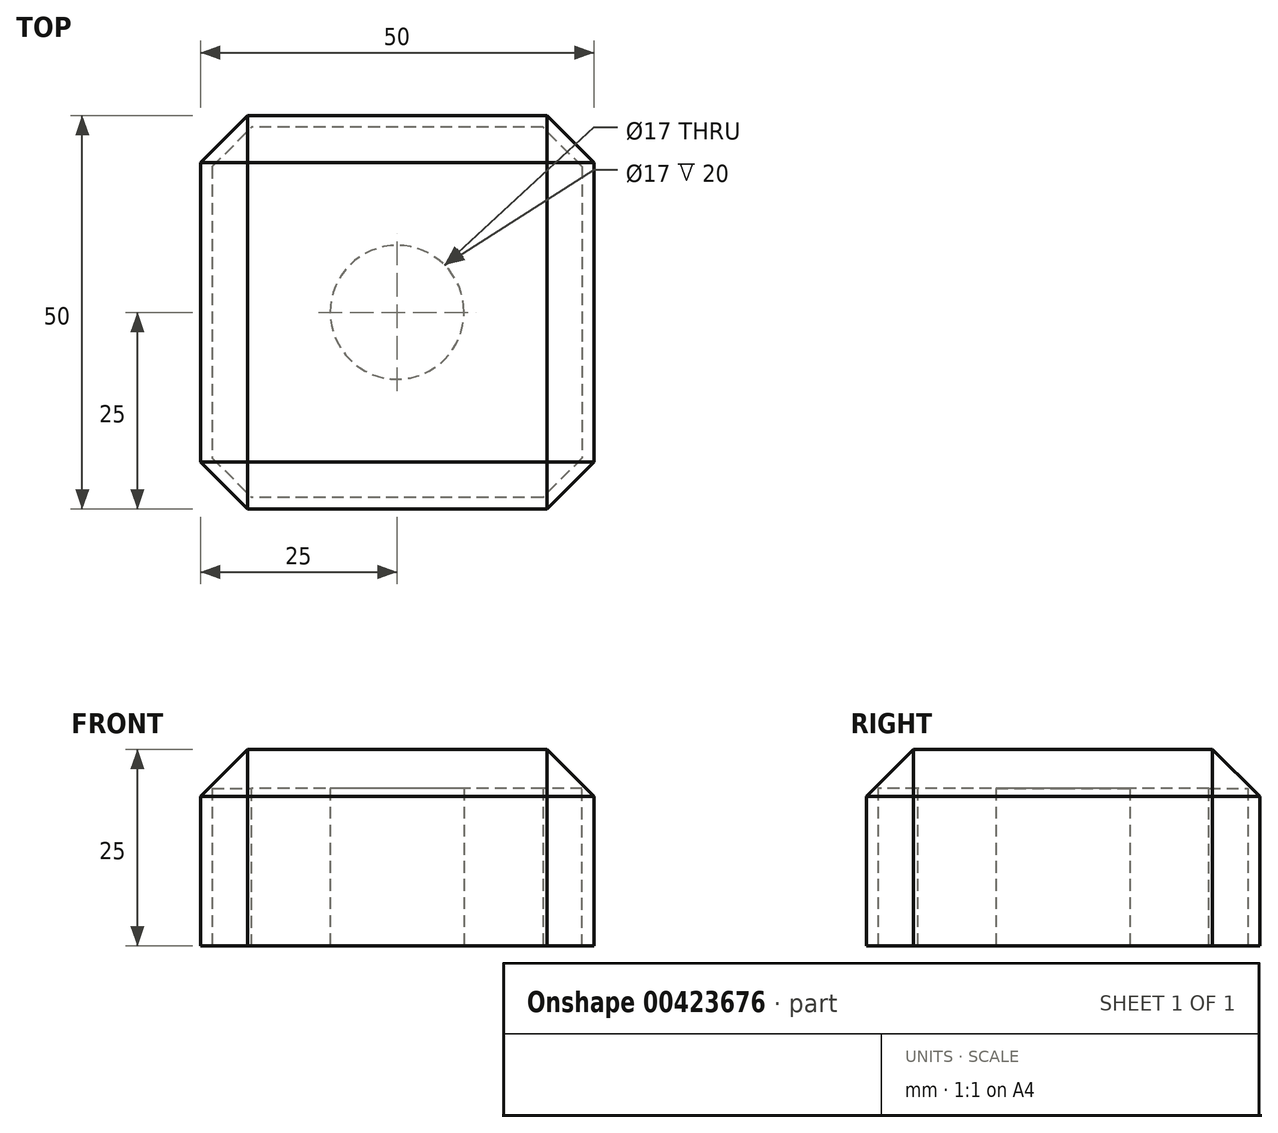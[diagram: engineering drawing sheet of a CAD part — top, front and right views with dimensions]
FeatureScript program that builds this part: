
annotation { "Feature Type Name" : "Feature", "Feature Type Description" : "" }
export const myFeature = defineFeature(function(context is Context, id is Id, definition is map)
    precondition{}
    {
        {
            var Q0;
            Q0=qCreatedBy(makeId("Top.planeOp"),FACE);
            var sketch = newSketch(context, id + "F0", { "sketchPlane" : qUnion([Q0])});
            skCircle(sketch, "E0", {"center": v(0, 0) * mm, "radius": 8.5 * mm});
            skLineSegment(sketch, "E1.bottom", {"start": v(23.5, 23.5) * mm, "end": v(-23.5, 23.5) * mm});
            skLineSegment(sketch, "E1.top", {"start": v(23.5, -23.5) * mm, "end": v(-23.5, -23.5) * mm});
            skLineSegment(sketch, "E1.left", {"start": v(23.5, 23.5) * mm, "end": v(23.5, -23.5) * mm});
            skLineSegment(sketch, "E1.right", {"start": v(-23.5, 23.5) * mm, "end": v(-23.5, -23.5) * mm});
            skSolve(sketch);
        }
        {
            var Q0;
            Q0=qCreatedBy(makeId("Top.planeOp"),FACE);
            var sketch = newSketch(context, id + "F1", { "sketchPlane" : qUnion([Q0])});
            skLineSegment(sketch, "E2.bottom", {"start": v(25, 25) * mm, "end": v(-25, 25) * mm});
            skLineSegment(sketch, "E2.top", {"start": v(25, -25) * mm, "end": v(-25, -25) * mm});
            skLineSegment(sketch, "E2.left", {"start": v(25, 25) * mm, "end": v(25, -25) * mm});
            skLineSegment(sketch, "E2.right", {"start": v(-25, 25) * mm, "end": v(-25, -25) * mm});
            skPoint(sketch, "E2.middle", {"position": v(0, 0) * mm});
            skSolve(sketch);
        }
        {
            var Q0;
            Q0=qCreatedBy(makeId("Top.planeOp"),FACE);
            var sketch = newSketch(context, id + "F2", { "sketchPlane" : qUnion([Q0])});
            skCircle(sketch, "E3", {"center": v(0, 0) * mm, "radius": 8.5 * mm});
            skSolve(sketch);
        }
        {
            var Q0;
            Q0=makeQuery(id+"F1.imprint","IMPRINT",FACE,{"disambiguationData":[TD([[makeQuery(id+"F1.imprint","IMPRINT",EDGE,{"derivedFrom":sQuery(id+"F1.wireOp",EDGE,"E2.bottom")}),1.0]])]});
            var Q1;
            Q1 = qSketchRegion(id + "F1", true);
            extrude(context, id + "F3", {"entities" : qUnion([Q0, Q1]), "depth" : 25 * mm});
        }
        {
            var Q0;
            Q0 = qSketchRegion(id + "F0", true);
            extrude(context, id + "F4", {"entities" : qUnion([Q0]), "depth" : 20 * mm});
        }
        {
            var Q0;
            Q0 = qSketchRegion(id + "F2", true);
            extrude(context, id + "F5", {"entities" : qUnion([Q0]), "operationType" : NewBodyOperationType.REMOVE, "depth" : 20 * mm});
        }
        {
            var Q0;
            Q0=makeQuery(id+"F3.opExtrude","SWEPT_EDGE",EDGE,{"disambiguationData":[OSD([sQuery(id+"F1.wireOp",EDGE,"E2.bottom"),sQuery(id+"F1.wireOp",EDGE,"E2.right")])]});
            var Q1;
            Q1=makeQuery(id+"F3.opExtrude","CAP_EDGE",EDGE,{"disambiguationData":[OSD([sQuery(id+"F1.wireOp",EDGE,"E2.right")])],"isStart":false});
            var Q2;
            Q2=makeQuery(id+"F3.opExtrude","SWEPT_EDGE",EDGE,{"disambiguationData":[OSD([sQuery(id+"F1.wireOp",EDGE,"E2.top"),sQuery(id+"F1.wireOp",EDGE,"E2.right")])]});
            var Q3;
            Q3=makeQuery(id+"F3.opExtrude","SWEPT_EDGE",EDGE,{"disambiguationData":[OSD([sQuery(id+"F1.wireOp",EDGE,"E2.top"),sQuery(id+"F1.wireOp",EDGE,"E2.left")])]});
            var Q4;
            Q4=makeQuery(id+"F3.opExtrude","SWEPT_EDGE",EDGE,{"disambiguationData":[OSD([sQuery(id+"F1.wireOp",EDGE,"E2.bottom"),sQuery(id+"F1.wireOp",EDGE,"E2.left")])]});
            var Q5;
            Q5=makeQuery(id+"F3.opExtrude","CAP_EDGE",EDGE,{"disambiguationData":[OSD([sQuery(id+"F1.wireOp",EDGE,"E2.bottom")])],"isStart":false});
            var Q6;
            Q6=makeQuery(id+"F3.opExtrude","CAP_EDGE",EDGE,{"disambiguationData":[OSD([sQuery(id+"F1.wireOp",EDGE,"E2.top")])],"isStart":false});
            var Q7;
            Q7=makeQuery(id+"F3.opExtrude","CAP_EDGE",EDGE,{"disambiguationData":[OSD([sQuery(id+"F1.wireOp",EDGE,"E2.left")])],"isStart":false});
            chamfer(context, id + "F6", {"entities" : qUnion([Q0, Q1, Q2, Q3, Q4, Q5, Q6, Q7]), "width" : 6 * mm, "tangentPropagation" : true});
        }
        {
            var Q0;
            Q0=makeQuery(id+"F4.opExtrude","SWEPT_EDGE",EDGE,{"disambiguationData":[OSD([sQuery(id+"F0.wireOp",EDGE,"E1.bottom"),sQuery(id+"F0.wireOp",EDGE,"E1.left")])]});
            var Q1;
            Q1=makeQuery(id+"F4.opExtrude","SWEPT_EDGE",EDGE,{"disambiguationData":[OSD([sQuery(id+"F0.wireOp",EDGE,"E1.bottom"),sQuery(id+"F0.wireOp",EDGE,"E1.right")])]});
            var Q2;
            Q2=makeQuery(id+"F4.opExtrude","SWEPT_EDGE",EDGE,{"disambiguationData":[OSD([sQuery(id+"F0.wireOp",EDGE,"E1.top"),sQuery(id+"F0.wireOp",EDGE,"E1.right")])]});
            var Q3;
            Q3=makeQuery(id+"F4.opExtrude","SWEPT_EDGE",EDGE,{"disambiguationData":[OSD([sQuery(id+"F0.wireOp",EDGE,"E1.top"),sQuery(id+"F0.wireOp",EDGE,"E1.left")])]});
            chamfer(context, id + "F7", {"entities" : qUnion([Q0, Q1, Q2, Q3]), "width" : 5 * mm, "tangentPropagation" : true});
        }
    });
